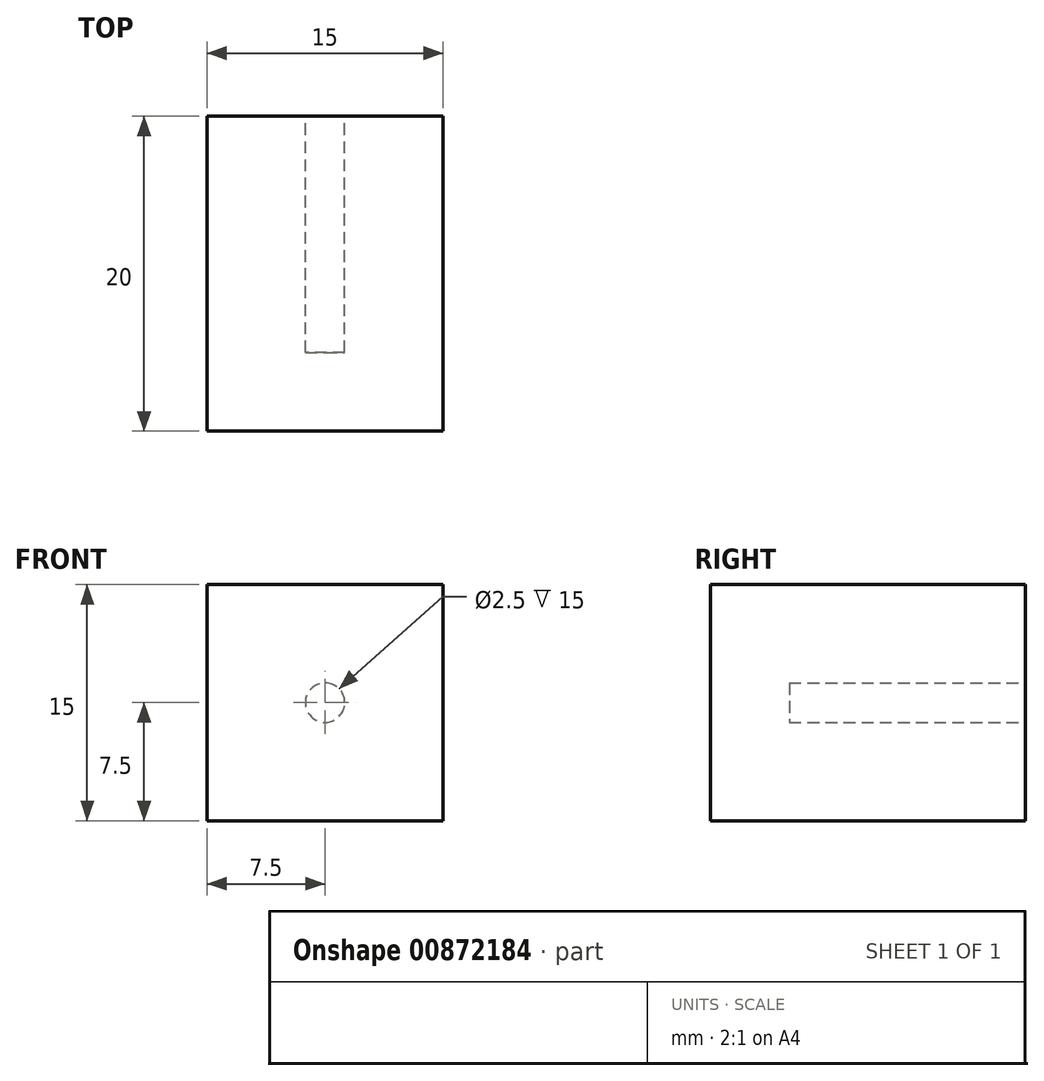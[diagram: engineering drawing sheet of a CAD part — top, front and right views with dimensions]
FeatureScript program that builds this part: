
annotation { "Feature Type Name" : "Feature", "Feature Type Description" : "" }
export const myFeature = defineFeature(function(context is Context, id is Id, definition is map)
    precondition{}
    {
        {
            var Q0;
            Q0=qCreatedBy(makeId("Top.planeOp"),FACE);
            var sketch = newSketch(context, id + "F0", { "sketchPlane" : qUnion([Q0])});
            skLineSegment(sketch, "E0.bottom", {"start": v(0, 0) * mm, "end": v(15, 0) * mm});
            skLineSegment(sketch, "E0.top", {"start": v(0, -20) * mm, "end": v(15, -20) * mm});
            skLineSegment(sketch, "E0.left", {"start": v(0, 0) * mm, "end": v(0, -20) * mm});
            skLineSegment(sketch, "E0.right", {"start": v(15, 0) * mm, "end": v(15, -20) * mm});
            skSolve(sketch);
        }
        {
            var Q0;
            Q0=makeQuery(id+"F0.imprint","IMPRINT",FACE,{"disambiguationData":[TD([[makeQuery(id+"F0.imprint","IMPRINT",EDGE,{"derivedFrom":sQuery(id+"F0.wireOp",EDGE,"E0.bottom")}),-1.0]])]});
            extrude(context, id + "F1", {"entities" : qUnion([Q0]), "depth" : 15 * mm, "offsetDistance" : 25 * mm});
        }
        {
            var Q0;
            Q0=makeQuery(id+"F1.opExtrude","SWEPT_FACE",FACE,{"disambiguationData":[OSD([sQuery(id+"F0.wireOp",EDGE,"E0.bottom")])]});
            var sketch = newSketch(context, id + "F2", { "sketchPlane" : qUnion([Q0])});
            skLineSegment(sketch, "E1", {"start": v(-7.5, 15) * mm, "end": v(-7.5, 0) * mm, "construction": true});
            skCircle(sketch, "E2", {"center": v(-7.5, 7.5) * mm, "radius": 1.25 * mm});
            skSolve(sketch);
        }
        {
            var Q0;
            Q0=makeQuery(id+"F2.imprint","IMPRINT",FACE,{"disambiguationData":[TD([[makeQuery(id+"F2.imprint","IMPRINT",EDGE,{"derivedFrom":sQuery(id+"F2.wireOp",EDGE,"E2")}),1.0]])]});
            extrude(context, id + "F3", {"entities" : qUnion([Q0]), "operationType" : NewBodyOperationType.REMOVE, "oppositeDirection" : true, "depth" : 15 * mm, "offsetDistance" : 25 * mm});
        }
    });
